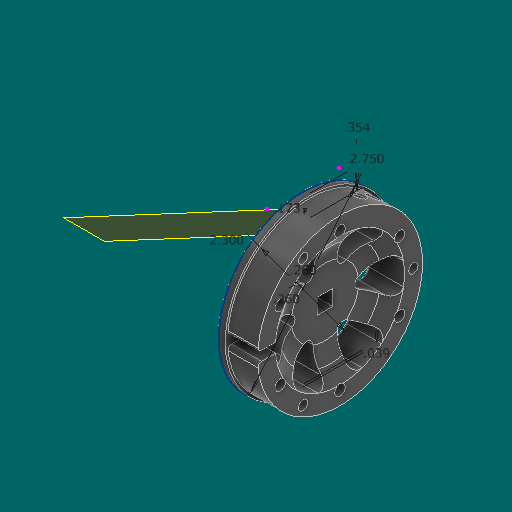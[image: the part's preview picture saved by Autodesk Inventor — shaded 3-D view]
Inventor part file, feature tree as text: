
AUTODESK INVENTOR PART (.ipt)
format: ipt  version: 2023.1 (Build 271208000, 208)  size: 1,211,904 bytes
history: native  units: in
note: dims shown in document units (in); Inventor stores cm internally (conversion verified against a paired STEP export)
features: extrude x8, sketch x7, fillet x5, other x5, pattern_circular x3, chamfer x3, revolve x1, plane x1
ambient origin geometry x8: Origin, YZ Plane, XZ Plane, XY Plane, X Axis, Y Axis, Z Axis, Center Point
bodies: Solid1 (feature_tree)
feature tree (33):
  sketch  "Sketch1"  dims[d0=2.75in d1=0.0394in]
  extrude  "Extrusion1"  Depth=0.0394in
  extrude  "Extrusion2"  Depth=0.5in TaperAngle=0.0deg
  extrude  "Extrusion3"  Depth=0.875in
  revolve  "Revolution1"  [1 undecoded]
  fillet  "Fillet5"  Radius=2.3622in
  sketch  "Sketch4"  dims[d9=0.3in d10=0.4in d11=2.3622in d13=360.0deg]
  extrude  "Extrusion4"  TaperAngle=45.0deg  [1 undecoded]
  extrude  "Extrusion5"  Depth=0.5in
  pattern_circular  "Circular Pattern4"  [2 undecoded]
  fillet  "Fillet7"  [1 undecoded]
  extrude  "Extrusion6"  Depth=0.0236in
  chamfer  "Chamfer1"  Distance=0.3543in
  fillet  "Fillet8"  Radius=0.1732in
  fillet  "Fillet9"  Radius=0.2431in
  pattern_circular  "Circular Pattern5"  [2 undecoded]
  extrude  "Extrusion8"  Depth=2.3622in TaperAngle=360.0deg
  chamfer  "Chamfer3"  Distance=0.0394in
  fillet  "Fillet10"  Radius=0.8937in
  plane  "Work Plane1"
  extrude  "Extrusion9"  Depth=0.1in
  chamfer  "Chamfer4"  Distance=0.1562in
  pattern_circular  "Circular Pattern7"  Count=3 Angle=360.0deg
  sketch  "Sketch2"  dims[d3=0.1181in d4=0.0in d5=0.5in d6=0.0in]
  sketch  "Sketch3"  dims[d7=0.875in d8=0.875in]
  sketch  "Sketch5"  dims[d15=0.0in d16=0.0in d17=45.0deg]
  sketch  "Sketch6"  dims[d18=0.0787in d19=0.5in]
  sketch  "Sketch7"  dims[d21=0.2405in d23=0.25in d24=360.0deg d35=0.0236in d41=0.3543in d42=0.1732in d43=0.2431in d44=0.0in d45=0.0in d46=0.0in d47=2.3622in d48=360.0deg d50=0.0394in d51=0.8937in d52=0.1in d53=0.1562in d55=1.1811in d57=360.0deg d59=0.2431in d60=0.0in d61=0.0472in d62=0.125in d63=45.0deg d67=0.26in d68=0.26in d69=2.3in d71=0.1in d72=0.125in d73=2.3622in d74=360.0deg d88=0.0591in d89=0.0787in d90=1.0in d91=0.0in d92=0.0472in d93=0.125in d94=45.0deg d95=0.5in d96=2.45in d97=0.1562in d98=1.0in d99=0.0in d100=0.0236in d101=0.125in d102=45.0deg d103=0.4466in d107=0.7874in d108=-0.0687in]
  other  "Work Axis1"
  other  "<userpath>\Documents\CAD\guardSwerve5\MainAssy.iam"
  other  "MainAssy.iam"
  other  "Bevel Gears:1"
  other  "Bevel Gear2:1"
note: 7 required parameter values undecoded (feature->parameter linkage not recoverable at this tier; creation-order binding heuristic only, values carry confidence <= 0.55)